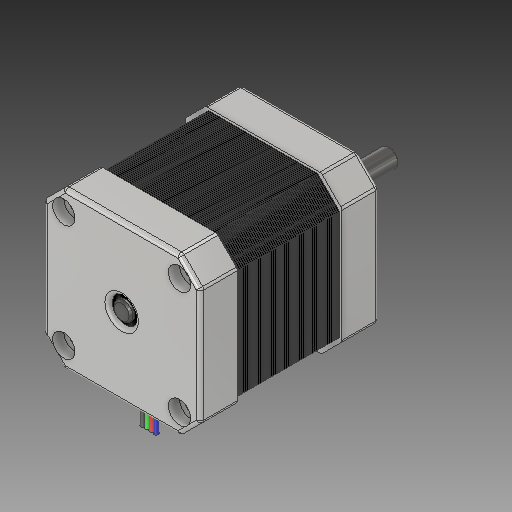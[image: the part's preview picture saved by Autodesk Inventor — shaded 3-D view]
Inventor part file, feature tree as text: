
AUTODESK INVENTOR PART (.ipt)
format: ipt  version: 2017 (Build 210142000, 142)  size: 1,354,752 bytes
history: native  units: mm
features: sketch x5, other x3
ambient origin geometry x8: Origin, YZ Plane, XZ Plane, XY Plane, X Axis, Y Axis, Z Axis, Center Point
bodies: Solid1 (feature_tree)
feature tree (8):
  other  "M1173041- NEMA 17.ipt"
  other  "Solid1::M1173041- NEMA 17.ipt"
  other  "TaggingFeature1"
  sketch  "Sketch1"  dims[d0=10.0mm]
  sketch  "Sketch4"
  sketch  "Sketch5"
  sketch  "Sketch6"
  sketch  "Sketch11"
